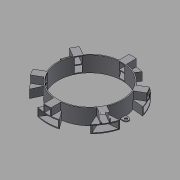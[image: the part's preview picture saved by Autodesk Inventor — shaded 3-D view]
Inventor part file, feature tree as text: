
AUTODESK INVENTOR PART (.ipt)
format: ipt  version: 2015 (Build 190159000, 159)  size: 369,664 bytes
history: native  units: mm
features: extrude x5, sketch x5, reference x4, plane x1
ambient origin geometry x8: Origin, YZ Plane, XZ Plane, XY Plane, X Axis, Y Axis, Z Axis, Center Point
bodies: Solid1 (feature_tree)
feature tree (15):
  extrude  "Extrusion1"  Depth=7.0mm TaperAngle=0.0deg
  extrude  "Extrusion2"  Depth=1.0mm TaperAngle=360.0deg
  sketch  "Sketch3"  dims[d31=7.0mm d32=0.0mm d35=1.0mm d36=0.0mm]
  extrude  "Extrusion4"  Depth=1.0mm TaperAngle=0.0deg
  extrude  "Extrusion5"  Depth=1.0mm
  plane  "Work Plane1"
  extrude  "Extrusion7"  [1 undecoded]
  sketch  "Sketch1"  dims[d10=60.0mm d12=360.0deg d15=7.0mm d16=0.0mm]
  sketch  "Sketch2"  dims[d18=1.0mm d19=0.0mm d27=60.0mm d29=360.0deg]
  sketch  "Sketch4"  dims[d60=1.0mm d61=0.0mm d62=1.0mm]
  sketch  "Sketch5"
  reference  "Reference7"
  reference  "Reference8"
  reference  "Reference9"
  reference  "Reference10"
note: 1 required parameter value undecoded (feature->parameter linkage not recoverable at this tier; creation-order binding heuristic only, values carry confidence <= 0.55)
